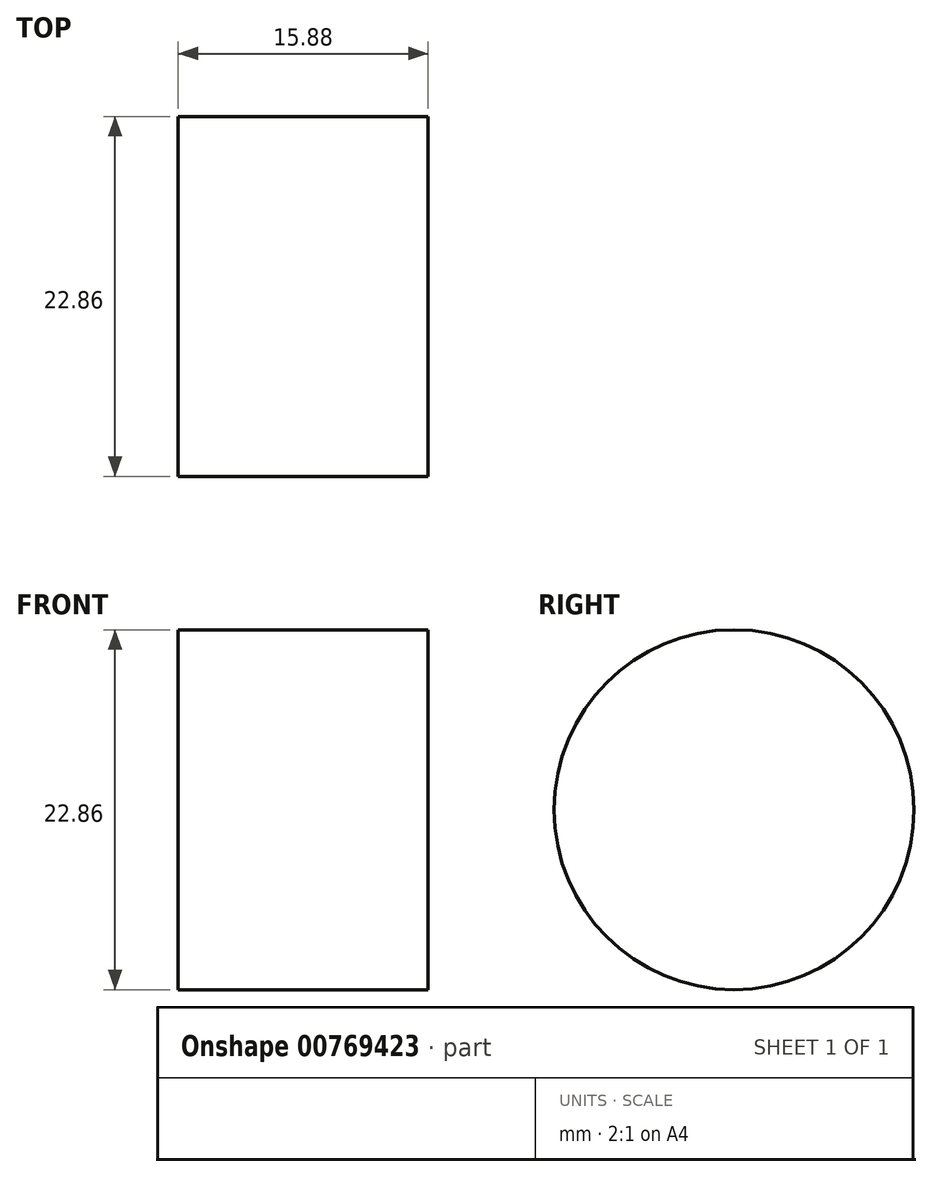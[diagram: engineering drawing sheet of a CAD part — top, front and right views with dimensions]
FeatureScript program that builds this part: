
annotation { "Feature Type Name" : "Feature", "Feature Type Description" : "" }
export const myFeature = defineFeature(function(context is Context, id is Id, definition is map)
    precondition{}
    {
        {
            var Q0;
            Q0=qCreatedBy(makeId("Right.planeOp"),FACE);
            var sketch = newSketch(context, id + "F0", { "sketchPlane" : qUnion([Q0])});
            skCircle(sketch, "E0", {"center": v(0, 0) * mm, "radius": 11.43 * mm});
            skSolve(sketch);
        }
        {
            var Q0;
            Q0=makeQuery(id+"F0.imprint","IMPRINT",FACE,{"disambiguationData":[TD([[makeQuery(id+"F0.imprint","IMPRINT",EDGE,{"derivedFrom":sQuery(id+"F0.wireOp",EDGE,"E0")}),1.0]])]});
            extrude(context, id + "F1", {"entities" : qUnion([Q0]), "depth" : 15.88 * mm, "offsetDistance" : 25.4 * mm});
        }
    });
